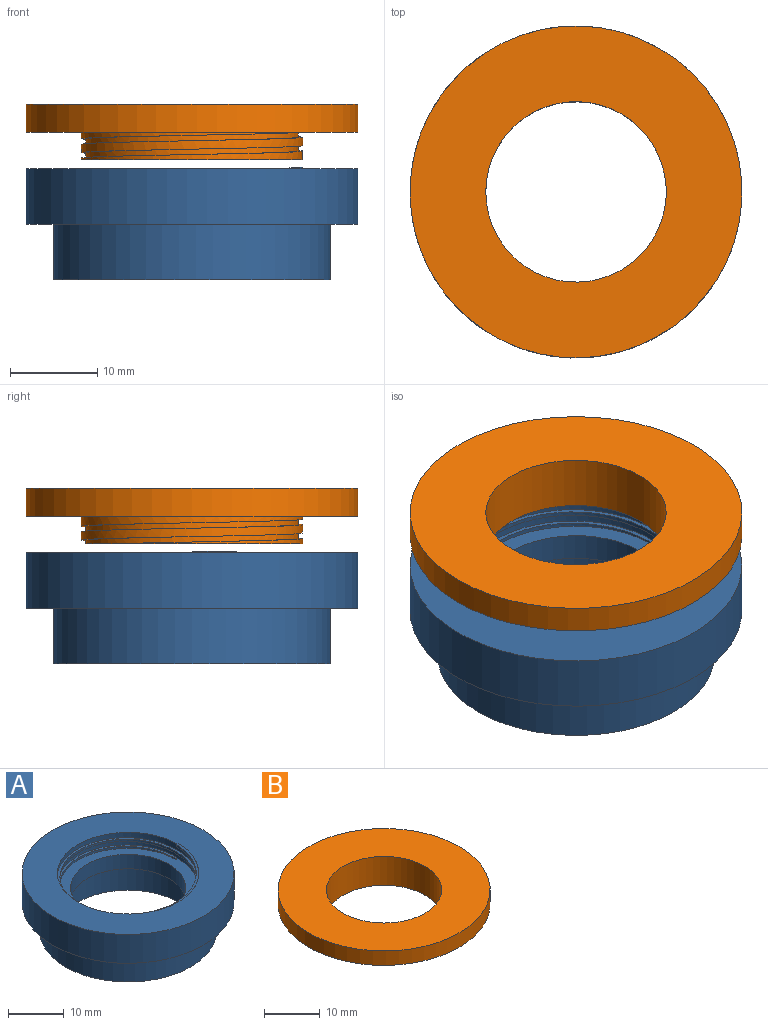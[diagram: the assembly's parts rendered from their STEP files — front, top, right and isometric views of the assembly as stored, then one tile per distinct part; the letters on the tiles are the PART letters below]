
ASSEMBLY  parts=2 mates=1
PART A: 16 faces, bbox 38.1x38.1x12.9 mm
  f0: cylinder r=12.7mm len=25.4mm, axis (0,0,1), area 181.4mm2, adj f4,f9,f10,f11,f12,f13
  f1: cylinder r=10.36mm len=20.71mm, axis (0,0,-1), area 206.6mm2, adj f2,f9
  f2: plane 25.4x25.4mm, normal (0,0,-1), area 169.7mm2, adj f1,f6
  f3: cylinder r=19.05mm len=38.1mm, axis (0,0,-1), area 760.1mm2, adj f4,f5
  f4: plane 38.1x38.1mm, normal (0,0,1), area 633.2mm2, adj f0,f3,f12,f13,f14
  f5: plane 38.1x38.1mm, normal (0,0,-1), area 348.4mm2, adj f3,f7
  f6: cylinder r=12.7mm len=25.4mm, axis (0,0,1), area 506.7mm2, adj f2,f8
  f7: cylinder r=15.88mm len=31.75mm, axis (0,0,1), area 633.4mm2, adj f5,f8
  f8: plane 31.75x31.75mm, normal (0,0,-1), area 285mm2, adj f6,f7
  f9: plane 25.4x25.4mm, normal (0,0,1), area 164mm2, adj f0,f1,f10,f11,f15
  f10: plane 0.46x0.21mm, normal (0,-1,0), area 0.1mm2, adj f0,f9,f13,f15
  f11: bspline ~29.36x25.43mm, area 65.7mm2, adj f0,f9,f12,f15
  f12: plane 0.47x0.47mm, normal (0,1,0), area 0.2mm2, adj f0,f4,f11,f13,f14,f15
  f13: bspline ~29.36x25.43mm, area 71.5mm2, adj f0,f4,f10,f12,f14,f15
  f14: cylinder r=12.71mm len=9.42mm, axis (0,0,1), area 1.1mm2, adj f4,f12,f13
  f15: cylinder r=12.24mm len=24.49mm, axis (0,0,1), area 70.5mm2, adj f9,f10,f11,f12,f13
PART B: 12 faces, bbox 38.1x38.1x6.4 mm
  f0: cylinder r=19.05mm len=38.1mm, axis (0,0,-1), area 380mm2, adj f1,f3
  f1: plane 38.1x38.1mm, normal (0,0,1), area 803.1mm2, adj f0,f11
  f2: cylinder r=12.7mm len=25.4mm, axis (0,0,1), area 159.3mm2, adj f3,f4,f5,f7,f9,f10
  f3: plane 38.1x38.1mm, normal (0,0,-1), area 631.2mm2, adj f0,f2,f5,f7,f8
  f4: plane 0.47x0.29mm, normal (0,1,0), area 0.1mm2, adj f2,f6,f7,f10
  f5: plane 0.62x0.62mm, normal (0,-1,0), area 0.3mm2, adj f2,f3,f6,f7,f8,f9
  f6: cylinder r=12.23mm len=24.45mm, axis (0,0,1), area 92.5mm2, adj f4,f5,f7,f9,f10
  f7: bspline ~29.67x25.69mm, area 76.3mm2, adj f2,f3,f4,f5,f6,f8
  f8: cylinder r=12.85mm len=11.72mm, axis (0,0,1), area 2.1mm2, adj f3,f5,f7
  f9: bspline ~29.67x25.69mm, area 66.3mm2, adj f2,f5,f6,f10
  f10: plane 25.4x25.4mm, normal (0,0,-1), area 162mm2, adj f2,f4,f6,f9,f11
  f11: cylinder r=10.36mm len=20.71mm, axis (0,0,1), area 413.2mm2, adj f1,f10
PLACE A t=(9.82,-6.43,-2.66)mm
PLACE B rot(axis=(0,0,1),60deg) t=(9.82,-6.43,-1.6)mm
MATE cylindrical B.f11 <-> A.f1  axis (0,0,-1) through (9.82,-6.43,4.75)mm
